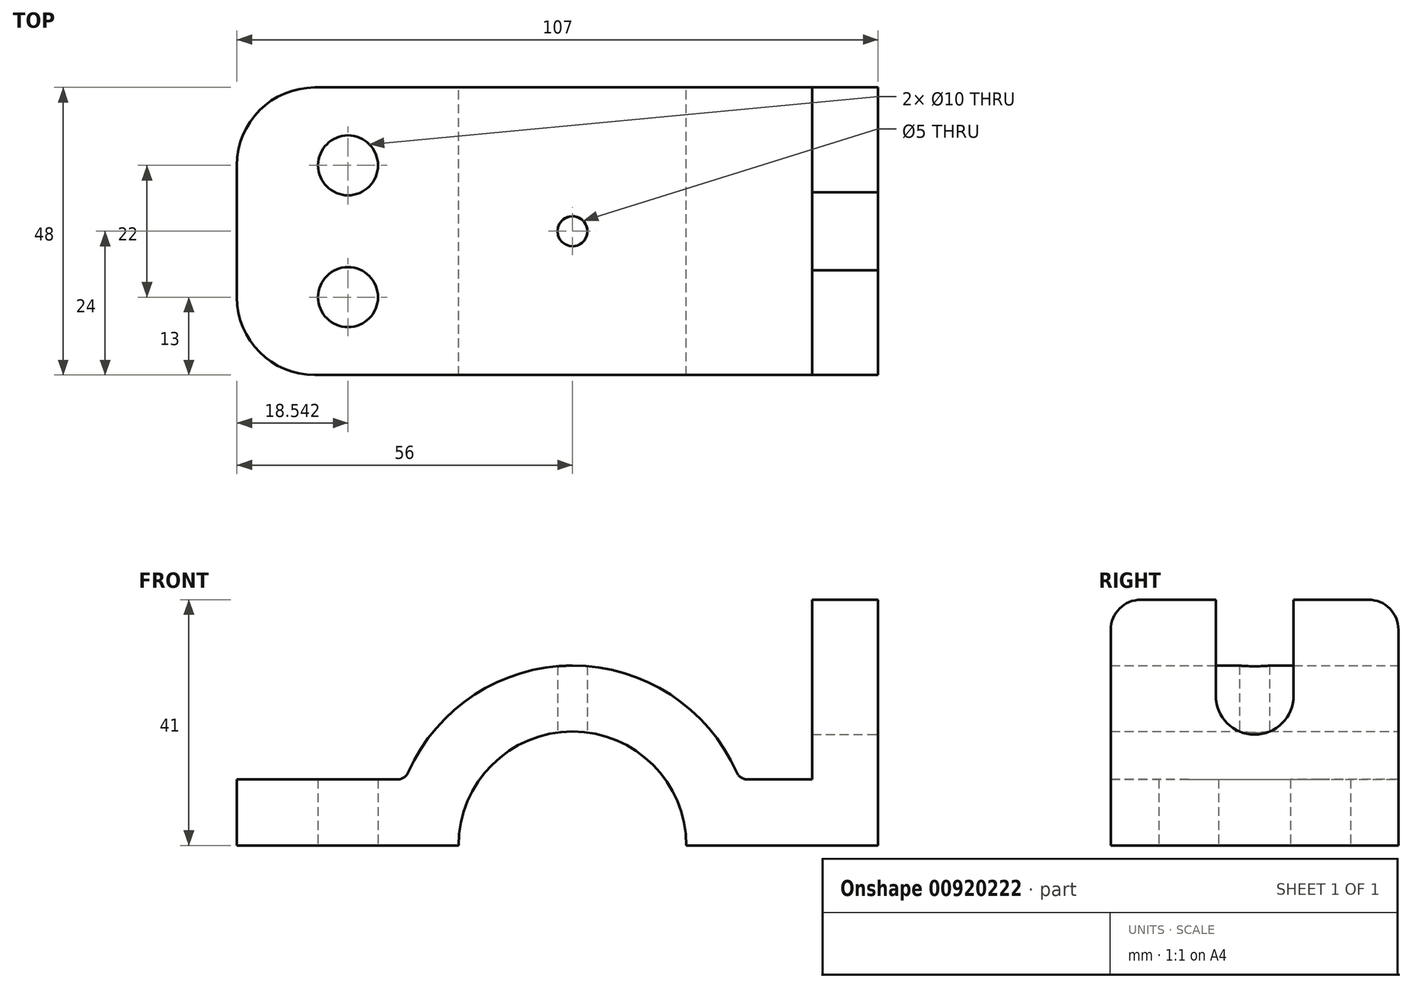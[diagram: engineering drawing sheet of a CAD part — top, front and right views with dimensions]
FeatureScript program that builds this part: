
annotation { "Feature Type Name" : "Feature", "Feature Type Description" : "" }
export const myFeature = defineFeature(function(context is Context, id is Id, definition is map)
    precondition{}
    {
        {
            var Q0;
            Q0=qCreatedBy(makeId("Front.planeOp"),FACE);
            var sketch = newSketch(context, id + "F0", { "sketchPlane" : qUnion([Q0])});
            skLineSegment(sketch, "E0", {"start": v(-56, 0) * mm, "end": v(51, 0) * mm});
            skLineSegment(sketch, "E1", {"start": v(0, 0) * mm, "end": v(51, 0) * mm, "construction": true});
            skLineSegment(sketch, "E2", {"start": v(-56, 11) * mm, "end": v(-56, 0) * mm});
            skLineSegment(sketch, "E3", {"start": v(51, 0) * mm, "end": v(51, 11) * mm});
            skLineSegment(sketch, "E4", {"start": v(-56, 11) * mm, "end": v(51, 11) * mm});
            skCircle(sketch, "E5", {"center": v(0, 0) * mm, "radius": 19 * mm});
            skCircle(sketch, "E6", {"center": v(0, 0) * mm, "radius": 30 * mm});
            skLineSegment(sketch, "E7", {"start": v(51, 41) * mm, "end": v(51, 11) * mm});
            skLineSegment(sketch, "E8", {"start": v(51, 41) * mm, "end": v(40, 41) * mm});
            skLineSegment(sketch, "E9", {"start": v(40, 41) * mm, "end": v(40, 11) * mm});
            skSolve(sketch);
        }
        {
            var Q0;
            {var subQ0=sQuery(id+"F0.wireOp",EDGE,"E2");Q0=makeQuery(id+"F0.imprint","IMPRINT",FACE,{"disambiguationData":[TD([[makeQuery(id+"F0.imprint","IMPRINT",EDGE,{"derivedFrom":subQ0}),1.0]])]});}
            var Q1;
            {var subQ0=sQuery(id+"F0.wireOp",EDGE,"E6");var subQ1=sQuery(id+"F0.wireOp",EDGE,"E0");var subQ2=makeQuery(id+"F0.imprint","INTERSECT",VERTEX,{"disambiguationData":[OD(0.0)],"derivedFrom":[subQ1,subQ0]});Q1=makeQuery(id+"F0.imprint","IMPRINT",FACE,{"disambiguationData":[TD([[makeQuery(id+"F0.imprint","IMPRINT",EDGE,{"disambiguationData":[TD([[subQ2,-1.0]])],"derivedFrom":subQ1}),1.0]])]});}
            var Q2;
            {var subQ0=sQuery(id+"F0.wireOp",EDGE,"E6");var subQ1=sQuery(id+"F0.wireOp",EDGE,"E4");var subQ2=makeQuery(id+"F0.imprint","INTERSECT",VERTEX,{"disambiguationData":[OD(0.0)],"derivedFrom":[subQ1,subQ0]});Q2=makeQuery(id+"F0.imprint","IMPRINT",FACE,{"disambiguationData":[TD([[makeQuery(id+"F0.imprint","IMPRINT",EDGE,{"disambiguationData":[TD([[subQ2,-1.0]])],"derivedFrom":subQ1}),1.0]])]});}
            var Q3;
            {var subQ0=sQuery(id+"F0.wireOp",EDGE,"E6");var subQ1=sQuery(id+"F0.wireOp",EDGE,"E0");var subQ2=makeQuery(id+"F0.imprint","INTERSECT",VERTEX,{"disambiguationData":[OD(1.0)],"derivedFrom":[subQ1,subQ0]});Q3=makeQuery(id+"F0.imprint","IMPRINT",FACE,{"disambiguationData":[TD([[makeQuery(id+"F0.imprint","IMPRINT",EDGE,{"disambiguationData":[TD([[subQ2,1.0]])],"derivedFrom":subQ1}),1.0]])]});}
            var Q4;
            {var subQ1=sQuery(id+"F0.wireOp",EDGE,"E3");Q4=makeQuery(id+"F0.imprint","IMPRINT",FACE,{"disambiguationData":[TD([[makeQuery(id+"F0.imprint","IMPRINT",EDGE,{"derivedFrom":subQ1}),1.0]])]});}
            var Q5;
            {var subQ0=sQuery(id+"F0.wireOp",EDGE,"E7");Q5=makeQuery(id+"F0.imprint","IMPRINT",FACE,{"disambiguationData":[TD([[makeQuery(id+"F0.imprint","IMPRINT",EDGE,{"derivedFrom":subQ0}),-1.0]])]});}
            extrude(context, id + "F1", {"entities" : qUnion([Q0, Q1, Q2, Q3, Q4, Q5]), "endBound" : BoundingType.SYMMETRIC, "depth" : 48 * mm, "offsetDistance" : 25 * mm});
        }
        {
            var Q0;
            Q0=makeQuery(id+"F1.opExtrude","SWEPT_FACE",FACE,{"disambiguationData":[OSD([sQuery(id+"F0.wireOp",EDGE,"E3"),sQuery(id+"F0.wireOp",EDGE,"E7")])]});
            var sketch = newSketch(context, id + "F2", { "sketchPlane" : qUnion([Q0])});
            skLineSegment(sketch, "E10", {"start": v(0, 0) * mm, "end": v(0, 25) * mm, "construction": true});
            skCircle(sketch, "E11", {"center": v(0, 25) * mm, "radius": 6.5 * mm});
            skLineSegment(sketch, "E12", {"start": v(6.5, 25) * mm, "end": v(6.5, 41) * mm});
            skLineSegment(sketch, "E13", {"start": v(-6.5, 25) * mm, "end": v(-6.5, 41) * mm});
            skLineSegment(sketch, "E14", {"start": v(-6.5, 41) * mm, "end": v(6.5, 41) * mm});
            skSolve(sketch);
        }
        {
            var Q0;
            {var subQ0=sQuery(id+"F2.wireOp",EDGE,"E11");var subQ1=makeQuery(id+"F2.imprint","INTERSECT",VERTEX,{"derivedFrom":[subQ0,sQuery(id+"F2.wireOp",EDGE,"E12")]});Q0=makeQuery(id+"F2.imprint","IMPRINT",FACE,{"disambiguationData":[TD([[makeQuery(id+"F2.imprint","IMPRINT",EDGE,{"disambiguationData":[TD([[subQ1,-1.0]])],"derivedFrom":subQ0}),1.0]])]});}
            var Q1;
            {var subQ0=sQuery(id+"F2.wireOp",EDGE,"E12");Q1=makeQuery(id+"F2.imprint","IMPRINT",FACE,{"disambiguationData":[TD([[makeQuery(id+"F2.imprint","IMPRINT",EDGE,{"derivedFrom":subQ0}),1.0]])]});}
            extrude(context, id + "F3", {"entities" : qUnion([Q0, Q1]), "operationType" : NewBodyOperationType.REMOVE, "oppositeDirection" : true, "depth" : 17.3 * mm, "offsetDistance" : 25 * mm});
        }
        {
            var Q0;
            Q0=qCreatedBy(makeId("Top.planeOp"),FACE);
            var sketch = newSketch(context, id + "F4", { "sketchPlane" : qUnion([Q0])});
            skPoint(sketch, "E15", {"position": v(0, 0) * mm});
            skLineSegment(sketch, "E16", {"start": v(-56, 0) * mm, "end": v(-18.9, 0) * mm, "construction": true});
            skLineSegment(sketch, "E17", {"start": v(-37.46, 11) * mm, "end": v(-37.46, 0) * mm, "construction": true});
            skPoint(sketch, "E17.startSnap0", {"position": v(-37.46, 0) * mm});
            skLineSegment(sketch, "E18.MirrorCS", {"start": v(-37.46, -11) * mm, "end": v(-37.46, 0) * mm, "construction": true});
            skPoint(sketch, "E19", {"position": v(-37.46, 11) * mm});
            skPoint(sketch, "E20", {"position": v(-37.46, -11) * mm});
            skSolve(sketch);
        }
        {
            var Q0;
            Q0=sQuery(id+"F4.wireOp",VERTEX,"E19");
            var Q1;
            Q1=sQuery(id+"F4.wireOp",VERTEX,"E20");
            var Q2;
            Q2=makeQuery(id+"F1.opExtrude","SWEPT_BODY",BODY,{"disambiguationData":[OSD([sQuery(id+"F0.wireOp",EDGE,"E0"),sQuery(id+"F0.wireOp",EDGE,"E2"),sQuery(id+"F0.wireOp",EDGE,"E3"),sQuery(id+"F0.wireOp",EDGE,"E4"),sQuery(id+"F0.wireOp",EDGE,"E5"),sQuery(id+"F0.wireOp",EDGE,"E6"),sQuery(id+"F0.wireOp",EDGE,"E7"),sQuery(id+"F0.wireOp",EDGE,"E8"),sQuery(id+"F0.wireOp",EDGE,"E9")])]});
            hole(context, id + "F5", {"style" : HoleStyle.SIMPLE, "endStyle" : HoleEndStyle.THROUGH, "oppositeDirection" : true, "holeDiameter" : 10 * mm, "majorDiameter" : 5 * mm, "isTappedThrough" : true, "tappedDepth" : 12 * mm, "tapClearance" : 3, "locations" : qUnion([Q0, Q1]), "scope" : qUnion([Q2])});
        }
        {
            var Q0;
            Q0=sQuery(id+"F4.wireOp",VERTEX,"E15");
            var Q1;
            Q1=makeQuery(id+"F1.opExtrude","SWEPT_BODY",BODY,{"disambiguationData":[OSD([sQuery(id+"F0.wireOp",EDGE,"E0"),sQuery(id+"F0.wireOp",EDGE,"E2"),sQuery(id+"F0.wireOp",EDGE,"E3"),sQuery(id+"F0.wireOp",EDGE,"E4"),sQuery(id+"F0.wireOp",EDGE,"E5"),sQuery(id+"F0.wireOp",EDGE,"E6"),sQuery(id+"F0.wireOp",EDGE,"E7"),sQuery(id+"F0.wireOp",EDGE,"E8"),sQuery(id+"F0.wireOp",EDGE,"E9")])]});
            hole(context, id + "F6", {"style" : HoleStyle.SIMPLE, "endStyle" : HoleEndStyle.THROUGH, "oppositeDirection" : true, "holeDiameter" : 5 * mm, "majorDiameter" : 5 * mm, "isTappedThrough" : true, "tappedDepth" : 12 * mm, "tapClearance" : 3, "locations" : qUnion([Q0]), "scope" : qUnion([Q1])});
        }
        {
            var Q0;
            Q0=makeQuery(id+"F1.opExtrude","CAP_EDGE",EDGE,{"disambiguationData":[OSD([sQuery(id+"F0.wireOp",EDGE,"E2")])],"isStart":false});
            var Q1;
            Q1=makeQuery(id+"F1.opExtrude","CAP_EDGE",EDGE,{"disambiguationData":[OSD([sQuery(id+"F0.wireOp",EDGE,"E2")])],"isStart":true});
            fillet(context, id + "F7", {"entities" : qUnion([Q0, Q1]), "radius" : 13 * mm, "tangentPropagation" : true, "allowEdgeOverflow" : false});
        }
        {
            var Q0;
            Q0=makeQuery(id+"F1.opExtrude","CAP_EDGE",EDGE,{"disambiguationData":[OSD([sQuery(id+"F0.wireOp",EDGE,"E8")])],"isStart":true});
            var Q1;
            Q1=makeQuery(id+"F1.opExtrude","CAP_EDGE",EDGE,{"disambiguationData":[OSD([sQuery(id+"F0.wireOp",EDGE,"E8")])],"isStart":false});
            fillet(context, id + "F8", {"entities" : qUnion([Q0, Q1]), "radius" : 5 * mm, "tangentPropagation" : true, "allowEdgeOverflow" : false});
        }
        {
            var Q0;
            {var subQ0=sQuery(id+"F0.wireOp",EDGE,"E6");var subQ1=sQuery(id+"F0.wireOp",EDGE,"E4");Q0=makeQuery(id+"F1.opExtrude","SWEPT_EDGE",EDGE,{"disambiguationData":[OSD([subQ1,subQ0]),TDD([makeQuery(id+"F0.imprint","INTERSECT",VERTEX,{"disambiguationData":[OD(1.0)],"derivedFrom":[subQ1,subQ0]})])]});}
            var Q1;
            {var subQ0=sQuery(id+"F0.wireOp",EDGE,"E6");var subQ1=sQuery(id+"F0.wireOp",EDGE,"E4");Q1=makeQuery(id+"F1.opExtrude","SWEPT_EDGE",EDGE,{"disambiguationData":[OSD([subQ1,subQ0]),TDD([makeQuery(id+"F0.imprint","INTERSECT",VERTEX,{"disambiguationData":[OD(0.0)],"derivedFrom":[subQ1,subQ0]})])]});}
            fillet(context, id + "F9", {"entities" : qUnion([Q0, Q1]), "radius" : 2 * mm, "tangentPropagation" : true, "allowEdgeOverflow" : false});
        }
    });
